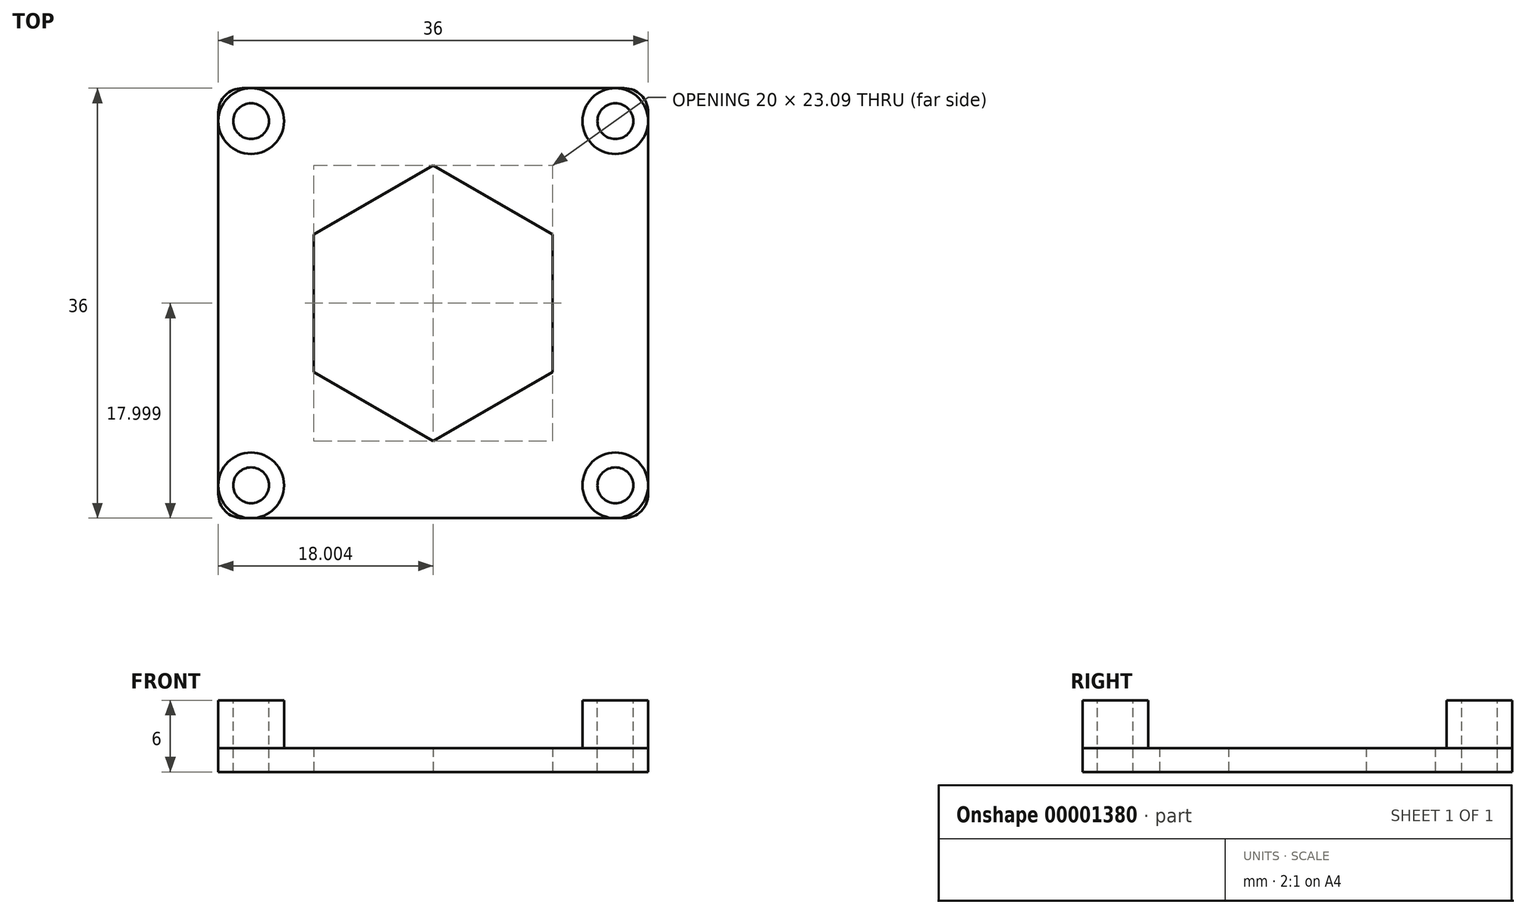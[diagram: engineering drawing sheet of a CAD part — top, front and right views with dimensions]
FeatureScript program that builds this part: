
annotation { "Feature Type Name" : "Feature", "Feature Type Description" : "" }
export const myFeature = defineFeature(function(context is Context, id is Id, definition is map)
    precondition{}
    {
        {
            var Q0;
            Q0=qCreatedBy(makeId("Top.planeOp"),FACE);
            var sketch = newSketch(context, id + "F0", { "sketchPlane" : qUnion([Q0])});
            skLineSegment(sketch, "E0.bottom", {"start": v(-40.66, 20.89) * mm, "end": v(-8.66, 20.89) * mm});
            skLineSegment(sketch, "E0.top", {"start": v(-40.66, -15.11) * mm, "end": v(-8.66, -15.11) * mm});
            skLineSegment(sketch, "E0.left", {"start": v(-42.66, 18.89) * mm, "end": v(-42.66, -13.11) * mm});
            skLineSegment(sketch, "E0.right", {"start": v(-6.66, 18.89) * mm, "end": v(-6.66, -13.11) * mm});
            skPoint(sketch, "E1.visualSharp", {"position": v(-42.66, 20.89) * mm});
            skArc(sketch, "E1.filletArc", {"start": v(-40.66, 20.89) * mm, "mid": v(-42.07, 20.3) * mm, "end": v(-42.66, 18.89) * mm});
            skPoint(sketch, "E2.visualSharp", {"position": v(-6.66, 20.89) * mm});
            skArc(sketch, "E2.filletArc", {"start": v(-6.66, 18.89) * mm, "mid": v(-7.24, 20.3) * mm, "end": v(-8.66, 20.89) * mm});
            skPoint(sketch, "E3.visualSharp", {"position": v(-6.66, -15.11) * mm});
            skArc(sketch, "E3.filletArc", {"start": v(-8.66, -15.11) * mm, "mid": v(-7.24, -14.53) * mm, "end": v(-6.66, -13.11) * mm});
            skPoint(sketch, "E4.visualSharp", {"position": v(-42.66, -15.11) * mm});
            skArc(sketch, "E4.filletArc", {"start": v(-42.66, -13.11) * mm, "mid": v(-42.07, -14.53) * mm, "end": v(-40.66, -15.11) * mm});
            skCircle(sketch, "E5.cCircle", {"center": v(-24.66, 2.89) * mm, "radius": 10 * mm, "construction": true});
            skLineSegment(sketch, "E5.0", {"start": v(-14.66, 8.66) * mm, "end": v(-14.66, -2.88) * mm});
            skLineSegment(sketch, "E5.1", {"start": v(-14.66, -2.88) * mm, "end": v(-24.66, -8.66) * mm});
            skLineSegment(sketch, "E5.2", {"start": v(-24.66, -8.66) * mm, "end": v(-34.66, -2.88) * mm});
            skLineSegment(sketch, "E5.3", {"start": v(-34.66, -2.88) * mm, "end": v(-34.66, 8.66) * mm});
            skLineSegment(sketch, "E5.4", {"start": v(-34.66, 8.66) * mm, "end": v(-24.66, 14.44) * mm});
            skLineSegment(sketch, "E5.5", {"start": v(-24.66, 14.44) * mm, "end": v(-14.66, 8.66) * mm});
            skPoint(sketch, "E5.0.midPoint", {"position": v(-14.66, 2.89) * mm});
            skSolve(sketch);
        }
        {
            var Q0;
            Q0=makeQuery(id+"F0.imprint","IMPRINT",FACE,{"disambiguationData":[TD([[makeQuery(id+"F0.imprint","IMPRINT",EDGE,{"derivedFrom":sQuery(id+"F0.wireOp",EDGE,"E0.bottom")}),-1.0]])]});
            extrude(context, id + "F1", {"entities" : qUnion([Q0]), "depth" : 2 * mm});
        }
        {
            var Q0;
            Q0=makeQuery(id+"F1.opExtrude","CAP_FACE",FACE,{"disambiguationData":[OSD([sQuery(id+"F0.wireOp",EDGE,"E0.bottom"),sQuery(id+"F0.wireOp",EDGE,"E0.top"),sQuery(id+"F0.wireOp",EDGE,"E0.left"),sQuery(id+"F0.wireOp",EDGE,"E0.right"),sQuery(id+"F0.wireOp",EDGE,"E1.filletArc"),sQuery(id+"F0.wireOp",EDGE,"E2.filletArc"),sQuery(id+"F0.wireOp",EDGE,"E3.filletArc"),sQuery(id+"F0.wireOp",EDGE,"E4.filletArc")])],"isStart":false});
            var sketch = newSketch(context, id + "F2", { "sketchPlane" : qUnion([Q0])});
            skCircle(sketch, "E6", {"center": v(-39.9, 18.14) * mm, "radius": 2.75 * mm});
            skCircle(sketch, "E7", {"center": v(-9.4, 18.14) * mm, "radius": 2.75 * mm});
            skCircle(sketch, "E8", {"center": v(-39.9, -12.36) * mm, "radius": 2.75 * mm});
            skCircle(sketch, "E9", {"center": v(-9.4, -12.36) * mm, "radius": 2.75 * mm});
            skSolve(sketch);
        }
        {
            var Q0;
            Q0 = qSketchRegion(id + "F2", true);
            extrude(context, id + "F3", {"entities" : qUnion([Q0]), "operationType" : NewBodyOperationType.ADD, "depth" : 4 * mm});
        }
        {
            var Q0;
            Q0=makeQuery(id+"F3.opExtrude","CAP_FACE",FACE,{"disambiguationData":[OSD([sQuery(id+"F2.wireOp",EDGE,"E6")])],"isStart":false});
            var sketch = newSketch(context, id + "F4", { "sketchPlane" : qUnion([Q0])});
            skCircle(sketch, "E10", {"center": v(-39.9, 18.14) * mm, "radius": 1.5 * mm});
            skCircle(sketch, "E11", {"center": v(-9.4, 18.14) * mm, "radius": 1.5 * mm});
            skCircle(sketch, "E12", {"center": v(-9.4, -12.36) * mm, "radius": 1.5 * mm});
            skCircle(sketch, "E13", {"center": v(-39.9, -12.36) * mm, "radius": 1.5 * mm});
            skSolve(sketch);
        }
        {
            var Q0;
            Q0 = qSketchRegion(id + "F4", true);
            extrude(context, id + "F5", {"entities" : qUnion([Q0]), "operationType" : NewBodyOperationType.REMOVE, "oppositeDirection" : true, "depth" : 25 * mm});
        }
    });
